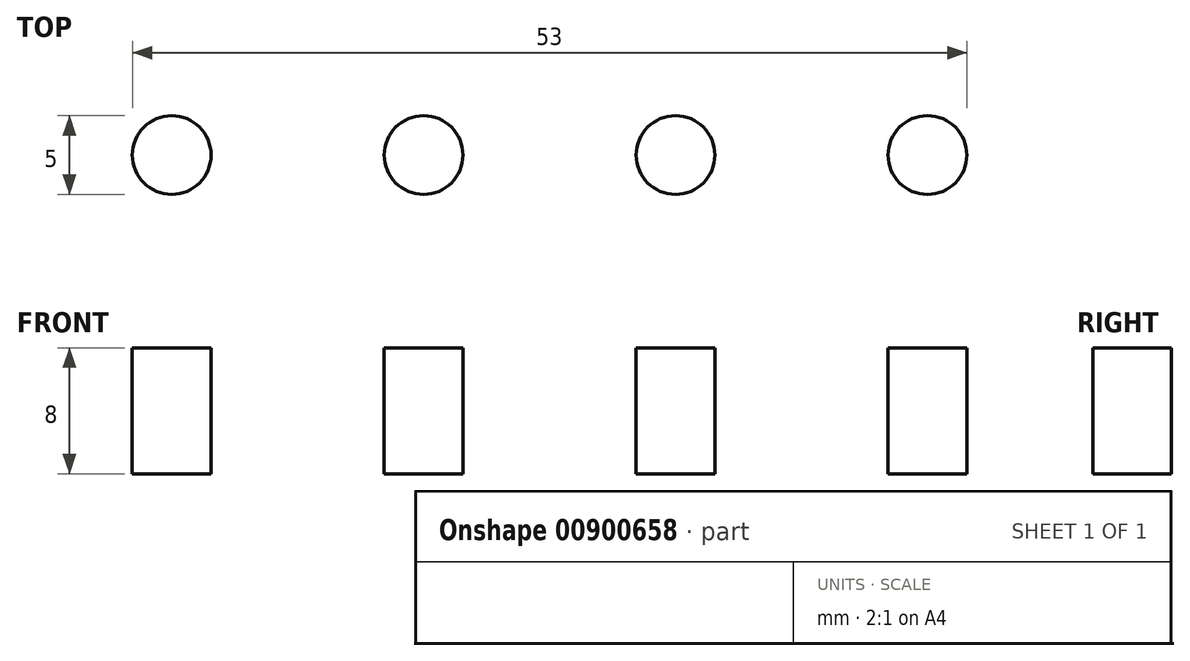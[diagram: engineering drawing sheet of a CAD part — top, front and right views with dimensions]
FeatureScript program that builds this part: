
annotation { "Feature Type Name" : "Feature", "Feature Type Description" : "" }
export const myFeature = defineFeature(function(context is Context, id is Id, definition is map)
    precondition{}
    {
        {
            var Q0;
            Q0=qCreatedBy(makeId("Top.planeOp"),FACE);
            var sketch = newSketch(context, id + "F0", { "sketchPlane" : qUnion([Q0])});
            skCircle(sketch, "E0", {"center": v(-13.9, -20.18) * mm, "radius": 2.5 * mm});
            skSolve(sketch);
        }
        {
            var Q0;
            Q0=qSketchRegion(id+"F0",true);
            extrude(context, id + "F1", {"entities" : qUnion([Q0]), "depth" : 8 * mm, "offsetDistance" : 25 * mm});
        }
        {
            var Q0;
            Q0=makeQuery(id+"F1.opExtrude","SWEPT_BODY",BODY,{"disambiguationData":[OSD([sQuery(id+"F0.wireOp",EDGE,"E0")])]});
            transform(context, id + "F2", {"entities" : qUnion([Q0]), "transformType" : TransformType.TRANSLATION_3D, "dx" : 16 * mm, "dy" : 0 * mm, "dz" : 0 * mm, "makeCopy" : true});
        }
        {
            var Q0;
            Q0=makeQuery(id+"F2.opPattern","COPY",BODY,{"derivedFrom":makeQuery(id+"F1.opExtrude","SWEPT_BODY",BODY,{"disambiguationData":[OSD([sQuery(id+"F0.wireOp",EDGE,"E0")])]}),"instanceName":"1"});
            transform(context, id + "F3", {"entities" : qUnion([Q0]), "transformType" : TransformType.TRANSLATION_3D, "dx" : 16 * mm, "dy" : 0 * mm, "dz" : 0 * mm, "makeCopy" : true});
        }
        {
            var Q0;
            Q0=makeQuery(id+"F3.opPattern","COPY",BODY,{"derivedFrom":makeQuery(id+"F2.opPattern","COPY",BODY,{"derivedFrom":makeQuery(id+"F1.opExtrude","SWEPT_BODY",BODY,{"disambiguationData":[OSD([sQuery(id+"F0.wireOp",EDGE,"E0")])]}),"instanceName":"1"}),"instanceName":"1"});
            transform(context, id + "F4", {"entities" : qUnion([Q0]), "transformType" : TransformType.TRANSLATION_3D, "dx" : 16 * mm, "dy" : 0 * mm, "dz" : 0 * mm, "makeCopy" : true});
        }
    });
